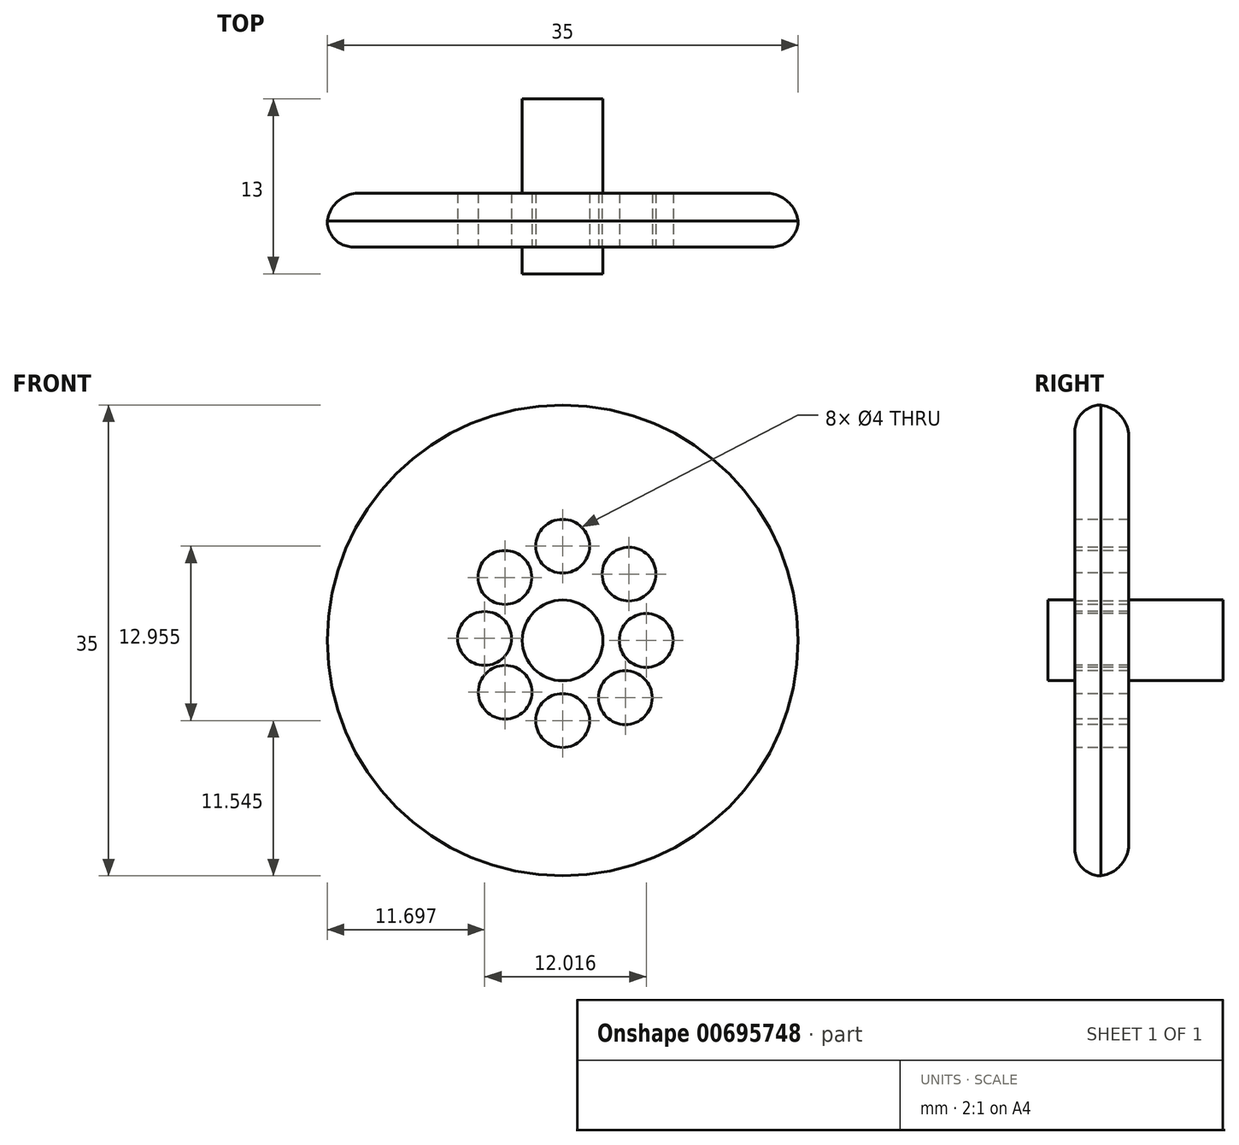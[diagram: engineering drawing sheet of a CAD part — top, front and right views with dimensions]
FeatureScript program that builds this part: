
annotation { "Feature Type Name" : "Feature", "Feature Type Description" : "" }
export const myFeature = defineFeature(function(context is Context, id is Id, definition is map)
    precondition{}
    {
        {
            var Q0;
            Q0=qCreatedBy(makeId("Front.planeOp"),FACE);
            var sketch = newSketch(context, id + "F0", { "sketchPlane" : qUnion([Q0])});
            skCircle(sketch, "E0", {"center": v(0, 0) * mm, "radius": 3 * mm});
            skSolve(sketch);
        }
        {
            var Q0;
            Q0=makeQuery(id+"F0.imprint","IMPRINT",FACE,{"disambiguationData":[TD([[makeQuery(id+"F0.imprint","IMPRINT",EDGE,{"derivedFrom":sQuery(id+"F0.wireOp",EDGE,"E0")}),1.0]])]});
            extrude(context, id + "F1", {"entities" : qUnion([Q0]), "oppositeDirection" : true, "depth" : 11 * mm, "offsetDistance" : 25 * mm});
        }
        {
            var Q0;
            Q0=qCreatedBy(makeId("Front.planeOp"),FACE);
            var sketch = newSketch(context, id + "F2", { "sketchPlane" : qUnion([Q0])});
            skCircle(sketch, "E1", {"center": v(0, 0) * mm, "radius": 17.5 * mm});
            skSolve(sketch);
        }
        {
            var Q0;
            Q0 = qSketchRegion(id + "F0", true);
            extrude(context, id + "F3", {"entities" : qUnion([Q0]), "operationType" : NewBodyOperationType.ADD, "depth" : 2 * mm, "offsetDistance" : 25 * mm});
        }
        {
            var Q0;
            Q0=makeQuery(id+"F2.imprint","IMPRINT",FACE,{"disambiguationData":[TD([[makeQuery(id+"F2.imprint","IMPRINT",EDGE,{"derivedFrom":sQuery(id+"F2.wireOp",EDGE,"E1")}),1.0]])]});
            extrude(context, id + "F4", {"entities" : qUnion([Q0]), "operationType" : NewBodyOperationType.ADD, "oppositeDirection" : true, "depth" : 4 * mm, "offsetDistance" : 25 * mm});
        }
        {
            var Q0;
            Q0=makeQuery(id+"F4.opExtrude","CAP_EDGE",EDGE,{"disambiguationData":[OSD([sQuery(id+"F2.wireOp",EDGE,"E1")])],"isStart":true});
            fillet(context, id + "F5", {"entities" : qUnion([Q0]), "radius" : 1.93 * mm, "tangentPropagation" : true, "allowEdgeOverflow" : false});
        }
        {
            var Q0;
            Q0=makeQuery(id+"F4.opExtrude","CAP_EDGE",EDGE,{"disambiguationData":[OSD([sQuery(id+"F2.wireOp",EDGE,"E1")])],"isStart":false});
            fillet(context, id + "F6", {"entities" : qUnion([Q0]), "radius" : 2.41 * mm, "tangentPropagation" : true, "allowEdgeOverflow" : false});
        }
        {
            var Q0;
            Q0=makeQuery(id+"F4.opExtrude","CAP_FACE",FACE,{"disambiguationData":[OSD([sQuery(id+"F2.wireOp",EDGE,"E1")])],"isStart":true});
            var sketch = newSketch(context, id + "F7", { "sketchPlane" : qUnion([Q0])});
            skCircle(sketch, "E2", {"center": v(0, 7) * mm, "radius": 2 * mm});
            skCircle(sketch, "E3", {"center": v(6.21, 0) * mm, "radius": 2 * mm});
            skCircle(sketch, "E4", {"center": v(4.93, 4.93) * mm, "radius": 2 * mm});
            skCircle(sketch, "E5", {"center": v(4.66, -4.26) * mm, "radius": 2 * mm});
            skCircle(sketch, "E6", {"center": v(0, -5.95) * mm, "radius": 2 * mm});
            skCircle(sketch, "E7", {"center": v(-4.28, -3.85) * mm, "radius": 2 * mm});
            skCircle(sketch, "E8", {"center": v(-5.8, 0.15) * mm, "radius": 2 * mm});
            skCircle(sketch, "E9", {"center": v(-4.3, 4.68) * mm, "radius": 2 * mm});
            skSolve(sketch);
        }
        {
            var Q0;
            Q0=makeQuery(id+"F7.imprint","IMPRINT",FACE,{"disambiguationData":[TD([[makeQuery(id+"F7.imprint","IMPRINT",EDGE,{"derivedFrom":sQuery(id+"F7.wireOp",EDGE,"E6")}),1.0]])]});
            var Q1;
            Q1=makeQuery(id+"F7.imprint","IMPRINT",FACE,{"disambiguationData":[TD([[makeQuery(id+"F7.imprint","IMPRINT",EDGE,{"derivedFrom":sQuery(id+"F7.wireOp",EDGE,"E3")}),1.0]])]});
            var Q2;
            Q2=makeQuery(id+"F7.imprint","IMPRINT",FACE,{"disambiguationData":[TD([[makeQuery(id+"F7.imprint","IMPRINT",EDGE,{"derivedFrom":sQuery(id+"F7.wireOp",EDGE,"E4")}),1.0]])]});
            var Q3;
            Q3=makeQuery(id+"F7.imprint","IMPRINT",FACE,{"disambiguationData":[TD([[makeQuery(id+"F7.imprint","IMPRINT",EDGE,{"derivedFrom":sQuery(id+"F7.wireOp",EDGE,"E2")}),1.0]])]});
            var Q4;
            Q4=makeQuery(id+"F7.imprint","IMPRINT",FACE,{"disambiguationData":[TD([[makeQuery(id+"F7.imprint","IMPRINT",EDGE,{"derivedFrom":sQuery(id+"F7.wireOp",EDGE,"E5")}),1.0]])]});
            var Q5;
            Q5=makeQuery(id+"F7.imprint","IMPRINT",FACE,{"disambiguationData":[TD([[makeQuery(id+"F7.imprint","IMPRINT",EDGE,{"derivedFrom":sQuery(id+"F7.wireOp",EDGE,"E7")}),1.0]])]});
            var Q6;
            Q6=makeQuery(id+"F7.imprint","IMPRINT",FACE,{"disambiguationData":[TD([[makeQuery(id+"F7.imprint","IMPRINT",EDGE,{"derivedFrom":sQuery(id+"F7.wireOp",EDGE,"E9")}),1.0]])]});
            var Q7;
            Q7=makeQuery(id+"F7.imprint","IMPRINT",FACE,{"disambiguationData":[TD([[makeQuery(id+"F7.imprint","IMPRINT",EDGE,{"derivedFrom":sQuery(id+"F7.wireOp",EDGE,"E8")}),1.0]])]});
            var Q8;
            Q8=sQuery(id+"F7.wireOp",EDGE,"E6");
            extrude(context, id + "F8", {"entities" : qUnion([Q0, Q1, Q2, Q3, Q4, Q5, Q6, Q7]), "operationType" : NewBodyOperationType.REMOVE, "surfaceEntities" : qUnion([Q8]), "oppositeDirection" : true, "depth" : 6.5 * mm, "offsetDistance" : 25 * mm});
        }
    });
